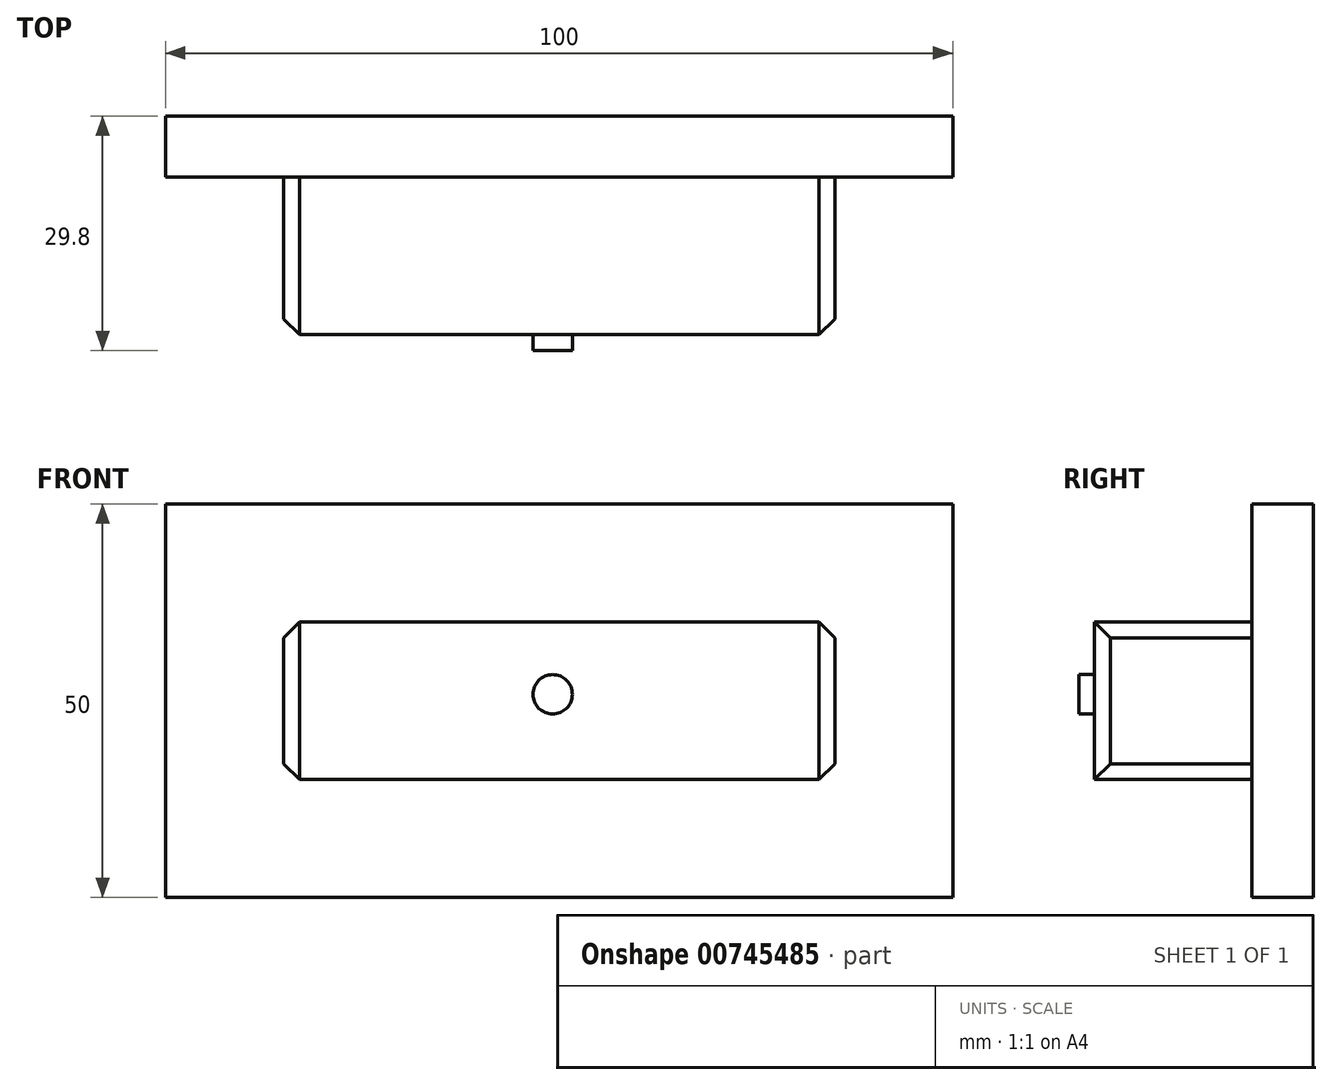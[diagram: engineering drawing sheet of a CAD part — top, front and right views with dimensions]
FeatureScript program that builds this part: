
annotation { "Feature Type Name" : "Feature", "Feature Type Description" : "" }
export const myFeature = defineFeature(function(context is Context, id is Id, definition is map)
    precondition{}
    {
        {
            var Q0;
            Q0=qCreatedBy(makeId("Front.planeOp"),FACE);
            var sketch = newSketch(context, id + "F0", { "sketchPlane" : qUnion([Q0])});
            skLineSegment(sketch, "E0.bottom", {"start": v(0, 0) * mm, "end": v(100, 0) * mm});
            skLineSegment(sketch, "E0.top", {"start": v(0, 50) * mm, "end": v(100, 50) * mm});
            skLineSegment(sketch, "E0.left", {"start": v(0, 0) * mm, "end": v(0, 50) * mm});
            skLineSegment(sketch, "E0.right", {"start": v(100, 0) * mm, "end": v(100, 50) * mm});
            skSolve(sketch);
        }
        {
            var Q0;
            Q0 = qSketchRegion(id + "F0", true);
            extrude(context, id + "F1", {"entities" : qUnion([Q0]), "depth" : 7.8 * mm, "offsetDistance" : 25.4 * mm});
        }
        {
            var Q0;
            Q0=makeQuery(id+"F1.opExtrude","CAP_FACE",FACE,{"disambiguationData":[OSD([sQuery(id+"F0.wireOp",EDGE,"E0.bottom"),sQuery(id+"F0.wireOp",EDGE,"E0.top"),sQuery(id+"F0.wireOp",EDGE,"E0.left"),sQuery(id+"F0.wireOp",EDGE,"E0.right")])],"isStart":false});
            var sketch = newSketch(context, id + "F2", { "sketchPlane" : qUnion([Q0])});
            skLineSegment(sketch, "E1.bottom", {"start": v(15, 35) * mm, "end": v(85, 35) * mm});
            skLineSegment(sketch, "E1.top", {"start": v(15, 15) * mm, "end": v(85, 15) * mm});
            skLineSegment(sketch, "E1.left", {"start": v(15, 35) * mm, "end": v(15, 15) * mm});
            skLineSegment(sketch, "E1.right", {"start": v(85, 35) * mm, "end": v(85, 15) * mm});
            skSolve(sketch);
        }
        {
            var Q0;
            Q0 = qSketchRegion(id + "F2", true);
            extrude(context, id + "F3", {"entities" : qUnion([Q0]), "operationType" : NewBodyOperationType.ADD, "depth" : 20 * mm, "offsetDistance" : 25.4 * mm});
        }
        {
            var Q0;
            Q0=makeQuery(id+"F3.opExtrude","CAP_FACE",FACE,{"disambiguationData":[OSD([sQuery(id+"F2.wireOp",EDGE,"E1.bottom"),sQuery(id+"F2.wireOp",EDGE,"E1.top"),sQuery(id+"F2.wireOp",EDGE,"E1.left"),sQuery(id+"F2.wireOp",EDGE,"E1.right")])],"isStart":false});
            var sketch = newSketch(context, id + "F4", { "sketchPlane" : qUnion([Q0])});
            skSolve(sketch);
        }
        {
            var Q0;
            Q0=makeQuery(id+"F3.opExtrude","SWEPT_EDGE",EDGE,{"disambiguationData":[OSD([sQuery(id+"F2.wireOp",EDGE,"E1.top"),sQuery(id+"F2.wireOp",EDGE,"E1.right")])]});
            var Q1;
            Q1=makeQuery(id+"F3.opExtrude","SWEPT_EDGE",EDGE,{"disambiguationData":[OSD([sQuery(id+"F2.wireOp",EDGE,"E1.bottom"),sQuery(id+"F2.wireOp",EDGE,"E1.right")])]});
            var Q2;
            Q2=makeQuery(id+"F3.opExtrude","SWEPT_EDGE",EDGE,{"disambiguationData":[OSD([sQuery(id+"F2.wireOp",EDGE,"E1.top"),sQuery(id+"F2.wireOp",EDGE,"E1.left")])]});
            var Q3;
            Q3=makeQuery(id+"F3.opExtrude","SWEPT_EDGE",EDGE,{"disambiguationData":[OSD([sQuery(id+"F2.wireOp",EDGE,"E1.bottom"),sQuery(id+"F2.wireOp",EDGE,"E1.left")])]});
            var Q4;
            Q4=makeQuery(id+"F3.opExtrude","CAP_EDGE",EDGE,{"disambiguationData":[OSD([sQuery(id+"F2.wireOp",EDGE,"E1.left")])],"isStart":false});
            var Q5;
            Q5=makeQuery(id+"F3.opExtrude","CAP_EDGE",EDGE,{"disambiguationData":[OSD([sQuery(id+"F2.wireOp",EDGE,"E1.right")])],"isStart":false});
            chamfer(context, id + "F5", {"entities" : qUnion([Q0, Q1, Q2, Q3, Q4, Q5]), "width" : 2 * mm, "tangentPropagation" : true});
        }
        {
            var Q0;
            Q0=makeQuery(id+"F4.imprint","IMPRINT",FACE,{"disambiguationData":[TD([[makeQuery(id+"F4.imprint","IMPRINT",EDGE,{"derivedFrom":makeQuery(id+"F3.opExtrude","CAP_EDGE",EDGE,{"disambiguationData":[OSD([sQuery(id+"F2.wireOp",EDGE,"E1.bottom")])],"isStart":false})}),-1.0]])]});
            var sketch = newSketch(context, id + "F6", { "sketchPlane" : qUnion([Q0])});
            skCircle(sketch, "E2", {"center": v(49.17, 25.82) * mm, "radius": 2.5 * mm});
            skSolve(sketch);
        }
        {
            var Q0;
            Q0 = qSketchRegion(id + "F6", true);
            extrude(context, id + "F7", {"entities" : qUnion([Q0]), "operationType" : NewBodyOperationType.ADD, "depth" : 2 * mm, "offsetDistance" : 25.4 * mm});
        }
    });
